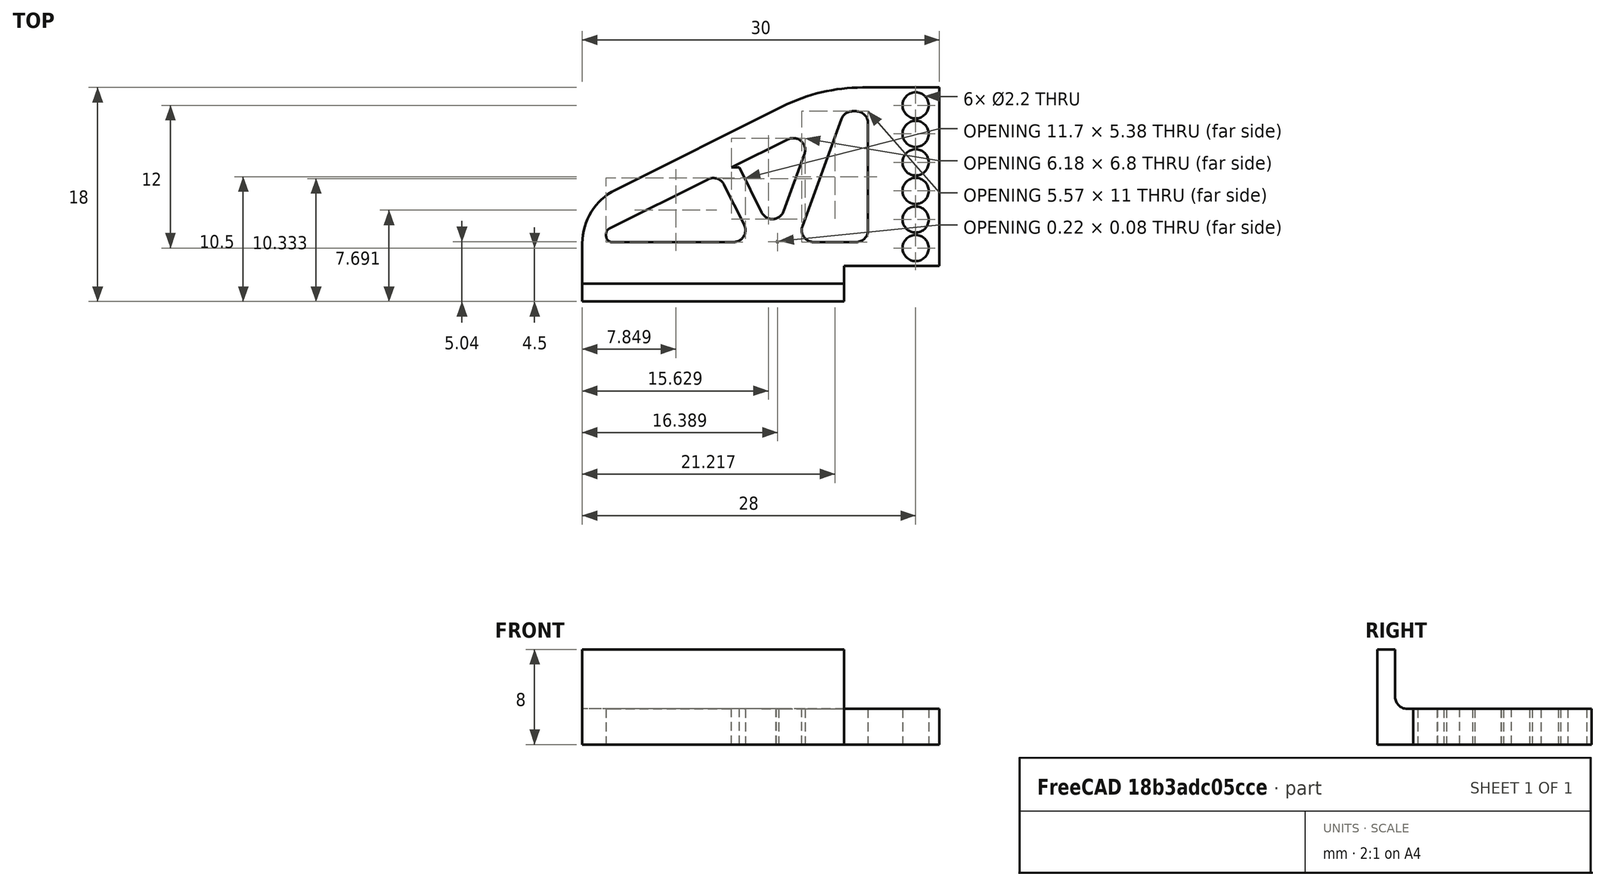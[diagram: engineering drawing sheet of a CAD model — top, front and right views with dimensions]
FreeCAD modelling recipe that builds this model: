
FCSTD DOCUMENT  (FreeCAD 0.18.1R)
Label: servohorn
License: All rights reserved
LicenseURL: http://en.wikipedia.org/wiki/All_rights_reserved
objects: Sketcher::SketchObject×11, PartDesign::Fillet×10, PartDesign::Pad×5, PartDesign::AdditivePipe×2, App::MaterialObjectPython×2, PartDesign::Pocket×1, PartDesign::Hole×1, PartDesign::LinearPattern×1, PartDesign::Body×1, Fem::ConstraintFixed×1, Fem::ConstraintForce×1, Fem::ConstraintPython×1, Fem::FemMeshObjectPython×1, App::FeaturePython×1, Fem::FemSolverObjectPython×1, Fem::FemAnalysis×1
note: 41 computed .brp shape members not serialized (recipe doc carries the construction recipe); baked Part::Feature solids carry a one-line shape summary decoded from their .brp

FEATURE [Sketcher::SketchObject] Sketch
  MapMode = 5
  Support = -> [XY_Plane]
  sketch-geometry (5):
    g0: LineSegment StartX=0 StartY=0 StartZ=0 EndX=30 EndY=0 EndZ=0
    g1: LineSegment StartX=30 StartY=0 StartZ=0 EndX=30 EndY=15 EndZ=0
    g2: LineSegment StartX=30 StartY=15 StartZ=0 EndX=20 EndY=15 EndZ=0
    g3: LineSegment StartX=20 StartY=15 StartZ=0 EndX=0 EndY=5 EndZ=0
    g4: LineSegment StartX=0 StartY=5 StartZ=0 EndX=0 EndY=0 EndZ=0
  constraints (14):
    c: Coincident(g-1,g0)
    c: PointOnObject(g0,g-1)
    c: Coincident(g0,g1)
    c: Vertical(g1)
    c: Coincident(g1,g2)
    c: Horizontal(g2)
    c: Coincident(g2,g3)
    c: PointOnObject(g3,g-2)
    c: Coincident(g4,g0)
    c: DistanceX(g0,g0) = 30
    c: DistanceY(g1,g1) = 15
    c: DistanceX(g0,g2) = 20
    c: DistanceY(g0,g3) = 5
    c: Coincident(g3,g4)
FEATURE [PartDesign::Pad] Pad
  Length = 3
  Length2 = 100
  Profile = -> Sketch
  Refine = true
  Type = 0
FEATURE [Sketcher::SketchObject] Sketch001
  ExternalGeometry = -> [Pad]
  MapMode = 5
  Placement = pos=(0,0,3) rot=(0,0,1;0rad)
  Support = -> [Pad]
  sketch-geometry (5):
    g0: LineSegment StartX=28 StartY=2 StartZ=0 EndX=28 EndY=13 EndZ=0
    g1: LineSegment StartX=28 StartY=13 StartZ=0 EndX=22 EndY=13 EndZ=0
    g2: LineSegment StartX=22 StartY=13 StartZ=0 EndX=2 EndY=3 EndZ=0
    g3: LineSegment StartX=2 StartY=3 StartZ=0 EndX=2 EndY=2 EndZ=0
    g4: LineSegment StartX=2 StartY=2 StartZ=0 EndX=28 EndY=2 EndZ=0
  constraints (15):
    c: Vertical(g0)
    c: Coincident(g0,g1)
    c: Horizontal(g1)
    c: Coincident(g1,g2)
    c: Coincident(g2,g3)
    c: Coincident(g3,g4)
    c: Coincident(g4,g0)
    c: Horizontal(g4)
    c: Vertical(g3)
    c: Parallel(g2,g-3)
    c: DistanceX(g-1,g3) = 2
    c: DistanceY(g-1,g3) = 2
    c: DistanceX(g0,g-5) = 2
    c: DistanceY(g0,g-5) = 2
    c: DistanceY(g2,g-6) = 2
FEATURE [PartDesign::Pocket] Pocket
  BaseFeature = -> Pad
  Length = 5
  Length2 = 100
  Profile = -> Sketch001
  Refine = true
  Type = 0
FEATURE [Sketcher::SketchObject] Sketch002
  ExternalGeometry = -> [Pocket]
  MapMode = 5
  Placement = pos=(0,0,0) rot=(1,0,0;1.5708rad)
  Support = -> [Pocket]
  sketch-geometry (4):
    g0: LineSegment StartX=0 StartY=3 StartZ=0 EndX=22 EndY=3 EndZ=0
    g1: LineSegment StartX=22 StartY=3 StartZ=0 EndX=22 EndY=0 EndZ=0
    g2: LineSegment StartX=22 StartY=0 StartZ=0 EndX=0 EndY=0 EndZ=0
    g3: LineSegment StartX=0 StartY=0 StartZ=0 EndX=0 EndY=3 EndZ=0
  constraints (11):
    c: Coincident(g0,g1)
    c: Coincident(g1,g2)
    c: Coincident(g2,g3)
    c: Coincident(g3,g0)
    c: Horizontal(g0)
    c: Horizontal(g2)
    c: Vertical(g1)
    c: Vertical(g3)
    c: Coincident(g0,g-4)
    c: PointOnObject(g1,g-5)
    c: DistanceX(g0,g-4) = 8
FEATURE [PartDesign::Pad] Pad001
  BaseFeature = -> Pocket
  Length = 3
  Length2 = 100
  Profile = -> Sketch002
  Refine = true
  Type = 0
FEATURE [Sketcher::SketchObject] Sketch003
  ExternalGeometry = -> [Pad001]
  MapMode = 5
  Placement = pos=(0,1e-16,3) rot=(0,0,1;0rad)
  Support = -> [Pad001]
  sketch-geometry (4):
    g0: LineSegment StartX=0 StartY=-3 StartZ=0 EndX=22 EndY=-3 EndZ=0
    g1: LineSegment StartX=22 StartY=-3 StartZ=0 EndX=22 EndY=-1.5 EndZ=0
    g2: LineSegment StartX=22 StartY=-1.5 StartZ=0 EndX=0 EndY=-1.5 EndZ=0
    g3: LineSegment StartX=0 StartY=-1.5 StartZ=0 EndX=0 EndY=-3 EndZ=0
  constraints (11):
    c: Coincident(g0,g1)
    c: Coincident(g1,g2)
    c: Coincident(g2,g3)
    c: Coincident(g3,g0)
    c: Horizontal(g0)
    c: Horizontal(g2)
    c: Vertical(g1)
    c: Vertical(g3)
    c: Coincident(g0,g-4)
    c: PointOnObject(g1,g-5)
    c: DistanceY(g0,g2) = 1.5
FEATURE [Sketcher::SketchObject] Sketch004
  ExternalGeometry = -> [Pad001,Sketch001]
  MapMode = 5
  Placement = pos=(0,2,0) rot=(0,0.707107,0.707107;3.14159rad)
  Support = -> [Pad001]
  sketch-geometry (4):
    g0: LineSegment StartX=-18 StartY=3 StartZ=0 EndX=-16.5 EndY=3 EndZ=0
    g1: LineSegment StartX=-16.5 StartY=3 StartZ=0 EndX=-16.5 EndY=0 EndZ=0
    g2: LineSegment StartX=-16.5 StartY=0 StartZ=0 EndX=-18 EndY=0 EndZ=0
    g3: LineSegment StartX=-18 StartY=0 StartZ=0 EndX=-18 EndY=3 EndZ=0
  constraints (12):
    c: Coincident(g0,g1)
    c: Coincident(g1,g2)
    c: Coincident(g2,g3)
    c: Coincident(g3,g0)
    c: Horizontal(g0)
    c: Horizontal(g2)
    c: Vertical(g1)
    c: Vertical(g3)
    c: DistanceX(g0,g0) = 1.5
    c: PointOnObject(g0,g-6)
    c: PointOnObject(g2,g-3)
    c: DistanceX(g-6,g0) = 10
FEATURE [Sketcher::SketchObject] Sketch005
  ExternalGeometry = -> [Sketch004,Sketch001]
  MapMode = 5
  Placement = pos=(0,1e-16,3) rot=(0,0,1;0rad)
  Support = -> [Pad001]
  sketch-geometry (1):
    g0: LineSegment StartX=18 StartY=2 StartZ=0 EndX=22 EndY=13 EndZ=0
  constraints (2):
    c: Coincident(g0,g-5)
    c: Coincident(g0,g-10)
FEATURE [PartDesign::AdditivePipe] AdditivePipe
  AuxilleryCurvelinear = true
  AuxillerySpineTangent = false
  BaseFeature = -> Pad001
  Binormal = (0,0,0)
  Mode = 0
  Profile = -> Sketch004
  Refine = true
  Spine = -> Sketch005
  SpineTangent = false
  Transformation = 0
  Transition = 0
FEATURE [PartDesign::Pad] Pad002
  BaseFeature = -> AdditivePipe
  Length = 4
  Length2 = 100
  Profile = -> AdditivePipe [Face14]
  Refine = true
  Type = 0
FEATURE [Sketcher::SketchObject] Sketch006
  ExternalGeometry = -> [Pad001,Sketch001]
  MapMode = 5
  Placement = pos=(0,2,0) rot=(0,0.707107,0.707107;3.14159rad)
  Support = -> [Pad001]
  sketch-geometry (4):
    g0: LineSegment StartX=-16 StartY=3 StartZ=0 EndX=-15.5 EndY=3 EndZ=0
    g1: LineSegment StartX=-15.5 StartY=3 StartZ=0 EndX=-15.5 EndY=0 EndZ=0
    g2: LineSegment StartX=-15.5 StartY=0 StartZ=0 EndX=-16 EndY=0 EndZ=0
    g3: LineSegment StartX=-16 StartY=0 StartZ=0 EndX=-16 EndY=3 EndZ=0
  constraints (12):
    c: Coincident(g0,g1)
    c: Coincident(g1,g2)
    c: Coincident(g2,g3)
    c: Coincident(g3,g0)
    c: Horizontal(g0)
    c: Horizontal(g2)
    c: Vertical(g1)
    c: Vertical(g3)
    c: DistanceX(g0,g0) = 0.5
    c: PointOnObject(g0,g-6)
    c: PointOnObject(g2,g-3)
    c: DistanceX(g-6,g0) = 12
FEATURE [Sketcher::SketchObject] Sketch007
  ExternalGeometry = -> [AdditivePipe]
  MapMode = 5
  Placement = pos=(0,0,3e-16) rot=(1,0,0;3.14159rad)
  Support = -> [AdditivePipe]
  sketch-geometry (2):
    g0: LineSegment StartX=15.02 StartY=-2 StartZ=0 EndX=11.885 EndY=-8.26993 EndZ=0
    g1: GeomPoint X=15.02 Y=-2 Z=0
  constraints (5):
    c: Perpendicular(g-4,g0)
    c: PointOnObject(g1,g-6)
    c: DistanceX(g1,g-5) = 1.48
    c: Coincident(g0,g1)
    c: Distance(g0) = 7.01
FEATURE [Sketcher::SketchObject] CopySketch006
  Placement = pos=(0,2,0) rot=(0,0.707107,0.707107;3.14159rad)
  sketch-geometry (4):
    g0: LineSegment StartX=-16.3178 StartY=3 StartZ=0 EndX=-14.3178 EndY=3 EndZ=0
    g1: LineSegment StartX=-14.3178 StartY=3 StartZ=0 EndX=-14.3178 EndY=0 EndZ=0
    g2: LineSegment StartX=-14.3178 StartY=0 StartZ=0 EndX=-16.3178 EndY=0 EndZ=0
    g3: LineSegment StartX=-16.3178 StartY=0 StartZ=0 EndX=-16.3178 EndY=3 EndZ=0
  constraints (9):
    c: Coincident(g0,g1)
    c: Coincident(g1,g2)
    c: Coincident(g2,g3)
    c: Coincident(g3,g0)
    c: Horizontal(g0)
    c: Horizontal(g2)
    c: Vertical(g1)
    c: Vertical(g3)
    c: DistanceX(g0,g0) = 2
FEATURE [PartDesign::AdditivePipe] AdditivePipe001
  AuxilleryCurvelinear = true
  AuxillerySpineTangent = false
  BaseFeature = -> Pad002
  Binormal = (0,0,0)
  Mode = 0
  Profile = -> CopySketch006
  Refine = true
  Spine = -> Sketch007
  SpineTangent = false
  Transformation = 0
  Transition = 0
FEATURE [Sketcher::SketchObject] Sketch008
  MapMode = 5
  Placement = pos=(0,0,0) rot=(1,0,0;3.14159rad)
  sketch-geometry (1):
    g0: LineSegment StartX=28 StartY=-15 StartZ=0 EndX=28 EndY=0 EndZ=0
  constraints (1):
    c: Vertical(g0)
FEATURE [PartDesign::Pad] Pad003
  BaseFeature = -> AdditivePipe001
  Length = 5
  Length2 = 100
  Profile = -> Sketch003
  Refine = true
  Type = 0
FEATURE [Sketcher::SketchObject] Sketch009
  ExternalGeometry = -> [Pad003]
  MapMode = 5
  Placement = pos=(0,0,3) rot=(0,0,1;0rad)
  sketch-geometry (1):
    g0: Circle CenterX=28 CenterY=13.5 CenterZ=0 NormalX=0 NormalY=0 NormalZ=1 AngleXU=0 Radius=1
  constraints (3):
    c: Diameter(g0) = 2
    c: DistanceY(g0,g-5) = 1.5
    c: DistanceX(g0,g-5) = 2
FEATURE [PartDesign::Hole] Hole
  BaseFeature = -> Pad003
  Depth = 25
  DepthType = 1
  Diameter = 2.2
  DrillPoint = 0
  DrillPointAngle = 118
  HoleCutCountersinkAngle = 90
  HoleCutDepth = 0
  HoleCutDiameter = 2
  HoleCutType = 0
  ModelActualThread = false
  Profile = -> Sketch009
  Refine = true
  Tapered = false
  TaperedAngle = 90
  ThreadAngle = 0
  ThreadClass = 0
  ThreadCutOffInner = 0
  ThreadCutOffOuter = 0
  ThreadDirection = 0
  ThreadFit = 0
  ThreadPitch = 0
  ThreadSize = 1
  ThreadType = 1
  Threaded = false
FEATURE [PartDesign::LinearPattern] LinearPattern
  BaseFeature = -> Hole
  Direction = -> Hole [Edge26]
  Length = 12
  Occurrences = 5
  Originals = -> [Hole]
  Refine = true
  Reversed = true
FEATURE [PartDesign::Fillet] Fillet
  Base = -> LinearPattern [Edge33]
  BaseFeature = -> LinearPattern
  Radius = 1
FEATURE [PartDesign::Fillet] Fillet001
  Base = -> Fillet [Edge64]
  BaseFeature = -> Fillet
  Radius = 0.5
FEATURE [PartDesign::Fillet] Fillet002
  Base = -> Fillet001 [Edge29]
  BaseFeature = -> Fillet001
  Radius = 0.5
FEATURE [PartDesign::Fillet] Fillet003
  Base = -> Fillet002 [Edge88,Edge87]
  BaseFeature = -> Fillet002
  Radius = 1
FEATURE [PartDesign::Fillet] Fillet004
  Base = -> Fillet003 [Edge36,Edge33]
  BaseFeature = -> Fillet003
  Radius = 1
FEATURE [PartDesign::Pad] Pad004
  BaseFeature = -> Fillet004
  Length = 0.5
  Length2 = 100
  Profile = -> Fillet004 [Face30]
  Refine = true
  Type = 0
FEATURE [PartDesign::Fillet] Fillet005
  Base = -> Pad004 [Edge92]
  BaseFeature = -> Pad004
  Radius = 1
FEATURE [PartDesign::Fillet] Fillet006
  Base = -> Fillet005 [Edge37]
  BaseFeature = -> Fillet005
  Radius = 1
FEATURE [PartDesign::Fillet] Fillet007
  Base = -> Fillet006 [Edge77,Edge74]
  BaseFeature = -> Fillet006
  Radius = 1
FEATURE [PartDesign::Fillet] Fillet008
  Base = -> Fillet007 [Edge79]
  BaseFeature = -> Fillet007
  Radius = 5
FEATURE [PartDesign::Fillet] Fillet009
  Base = -> Fillet008 [Edge42]
  BaseFeature = -> Fillet008
  Radius = 15
FEATURE [PartDesign::Body] Body
  Group = -> [Sketch,Pad,Sketch001,Pocket,Sketch002,Pad001,Sketch003,Sketch004,Sketch005,AdditivePipe,Pad002,Sketch007,AdditivePipe001,Sketch008,Pad003,Sketch009,Hole,LinearPattern,Fillet,Fillet001,Fillet002,Fillet003,Fillet004,Pad004,Fillet005,Fillet006,Fillet007,Fillet008,Fillet009]
  Origin = -> Origin
  Tip = -> Fillet009
FEATURE [App::MaterialObjectPython] SolidMaterial  # material (typed FeaturePython)
  Category = 0
  Material = Density=1240 kg/m^3,+12 more (map truncated)
  References = -> [Fillet009]
FEATURE [App::MaterialObjectPython] FluidMaterial  # material (typed FeaturePython)
  Category = 1
  Material = Density=1.20 kg/m^3,Description=Standard air properties at 20 Degrees Celsius and 1 atm,DynamicViscosity=1.80e-5 kg/m/s,+8 more (map truncated)
FEATURE [Fem::ConstraintFixed] FemConstraintFixed
  NormalDirection = (0,-1,2e-16)
  Normals = (9) [(0,-1,1.6e-16),(0,-1,1.6e-16),(0,-1,1.6e-16),(0,-1,1.6e-16),(0,-1,1.6e-16),(0,-1,1.6e-16),(0,-1,1.6e-16),(0,-1,1.6e-16),(0,-1,1.6e-16)]
  Points = (9) [(0,-3,8),(0,-3,4),(0,-3,8.88178e-16),(11,-3,8),(11,-3,4),(11,-3,8.88178e-16),(22,-3,8),(22,-3,4),(22,-3,8.88178e-16)]
  References = -> [Fillet009]
FEATURE [Fem::ConstraintForce] FemConstraintForce
  DirectionVector = (-1,0,0)
  Force = 10
  NormalDirection = (1,0,0)
  Points = (9) [(30,0,3),(30,7.5,3),(30,15,3),(30,0,1.5),(30,7.5,1.5),(30,15,1.5),(30,0,0),(30,7.5,0),(30,15,0)]
  References = -> [Fillet009]
  Reversed = true
FEATURE [Fem::ConstraintPython] ConstraintSelfWeight  # FEM object (typed FeaturePython)
  Gravity_x = 0
  Gravity_y = 0
  Gravity_z = -1
  NormalDirection = (0,0,1)
FEATURE [Fem::FemMeshObjectPython] FEMMeshGmsh  # FEM object (typed FeaturePython)
  Algorithm2D = 0
  Algorithm3D = 0
  CharacteristicLengthMax = 0
  CharacteristicLengthMin = 0
  CoherenceMesh = true
  ElementDimension = 0
  ElementOrder = 1
  GeometryTolerance = 1e-06
  GroupsOfNodes = false
  HighOrderOptimize = false
  OptimizeNetgen = false
  OptimizeStd = true
  Part = -> Fillet009
  RecombineAll = false
FEATURE [App::FeaturePython] Elasticity  # WARN: FeaturePython — macro-defined, semantics opaque (R4)
  BiCGstablDegree = 0
  Bubbles = false
  CalculatePangle = false
  CalculatePrincipal = false
  CalculateStrains = false
  CalculateStresses = false
  DoFrequencyAnalysis = false
  EigenmodesCount = 5
  LinearDirectMethod = 0
  LinearIterations = 500
  LinearIterativeMethod = 2
  LinearPreconditioning = 2
  LinearSolverType = 1
  LinearTolerance = 1e-08
  Priority = 10
  Stabilize = true
  SteadyStateTolerance = 1e-05
FEATURE [Fem::FemSolverObjectPython] SolverElmer  # FEM object (typed FeaturePython)
  Group = -> [Elasticity]
  SteadyStateMaxIterations = 1
  SteadyStateMinIterations = 0
FEATURE [Fem::FemAnalysis] Analysis
  Group = -> [SolidMaterial,FluidMaterial,FemConstraintFixed,FemConstraintForce,ConstraintSelfWeight,FEMMeshGmsh,SolverElmer]
